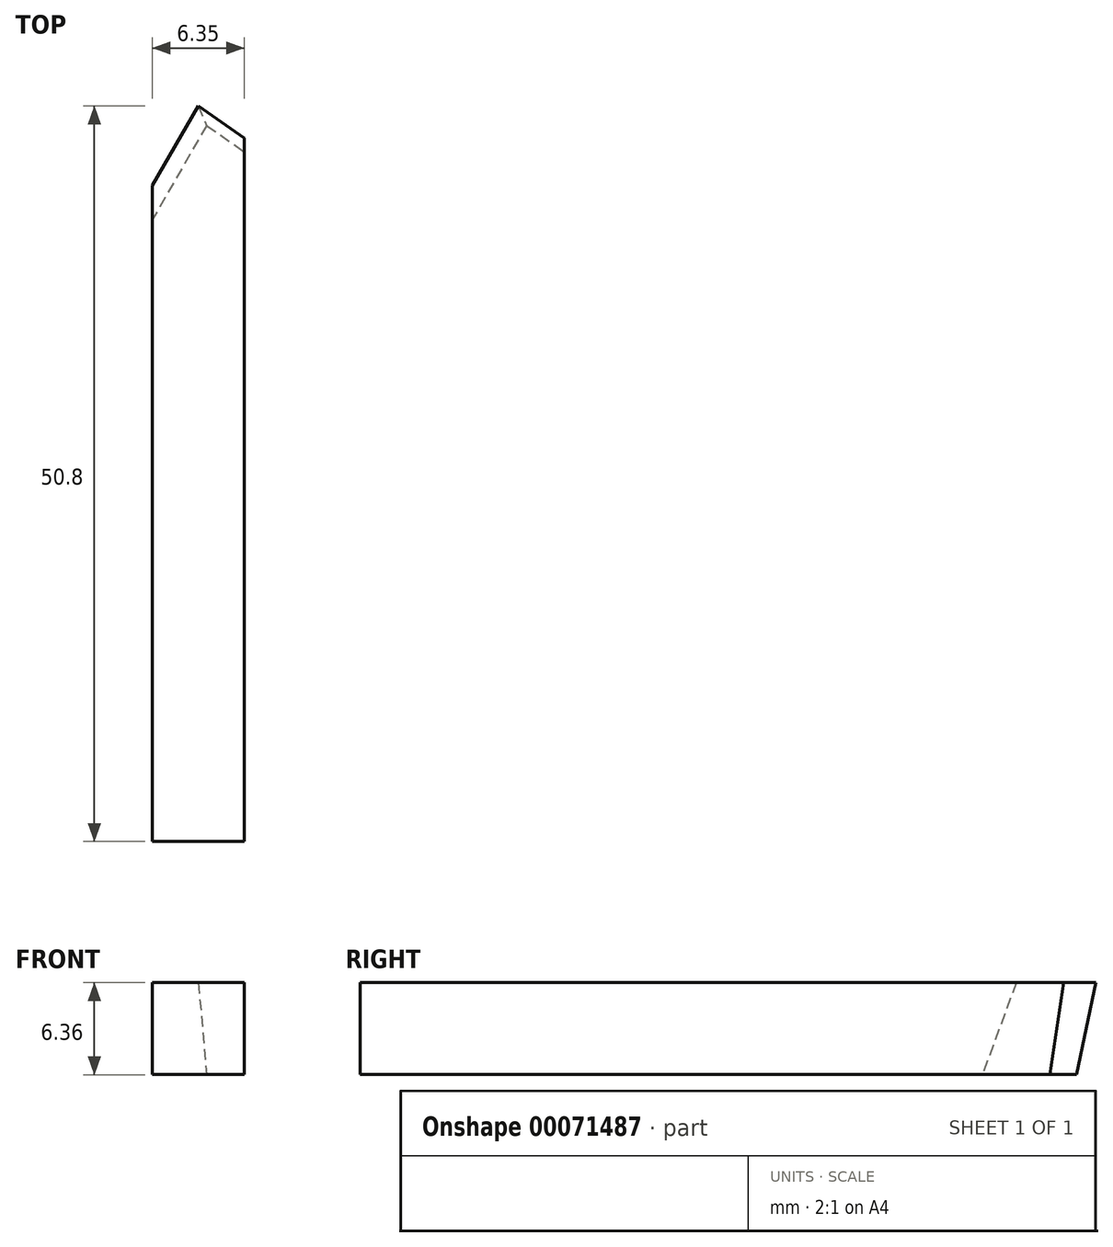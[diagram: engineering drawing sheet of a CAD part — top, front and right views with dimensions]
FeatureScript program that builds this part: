
annotation { "Feature Type Name" : "Feature", "Feature Type Description" : "" }
export const myFeature = defineFeature(function(context is Context, id is Id, definition is map)
    precondition{}
    {
        {
            var Q0;
            Q0=qCreatedBy(makeId("Front.planeOp"),FACE);
            var sketch = newSketch(context, id + "F0", { "sketchPlane" : qUnion([Q0])});
            skLineSegment(sketch, "E0.rect.bottom", {"start": v(3.18, 3.17) * mm, "end": v(-3.18, 3.17) * mm});
            skLineSegment(sketch, "E0.rect.top", {"start": v(3.18, -3.18) * mm, "end": v(-3.18, -3.18) * mm});
            skLineSegment(sketch, "E0.rect.left", {"start": v(3.18, 3.17) * mm, "end": v(3.18, -3.18) * mm});
            skLineSegment(sketch, "E0.rect.right", {"start": v(-3.18, 3.17) * mm, "end": v(-3.18, -3.18) * mm});
            skPoint(sketch, "E0.rect.middle", {"position": v(0, 0) * mm});
            skSolve(sketch);
        }
        {
            var Q0;
            Q0=makeQuery(id+"F0.imprint","IMPRINT",FACE,{"disambiguationData":[TD([[makeQuery(id+"F0.imprint","IMPRINT",EDGE,{"derivedFrom":sQuery(id+"F0.wireOp",EDGE,"E0.rect.bottom")}),1.0]])]});
            extrude(context, id + "F1", {"entities" : qUnion([Q0]), "depth" : 50.8 * mm});
        }
        {
            var Q0;
            Q0=makeQuery(id+"F1.opExtrude","SWEPT_FACE",FACE,{"disambiguationData":[OSD([sQuery(id+"F0.wireOp",EDGE,"E0.rect.bottom")])]});
            var sketch = newSketch(context, id + "F2", { "sketchPlane" : qUnion([Q0])});
            skLineSegment(sketch, "E1", {"start": v(0, 0) * mm, "end": v(-3.18, -5.5) * mm});
            skLineSegment(sketch, "E2", {"start": v(0, 0) * mm, "end": v(3.18, -2.22) * mm});
            skLineSegment(sketch, "E3", {"start": v(3.17, -2.22) * mm, "end": v(3.17, 0) * mm, "construction": true});
            skLineSegment(sketch, "E4", {"start": v(3.17, 0) * mm, "end": v(0, 0) * mm, "construction": true});
            skLineSegment(sketch, "E5", {"start": v(0, 0) * mm, "end": v(-3.18, 0) * mm});
            skLineSegment(sketch, "E6", {"start": v(-3.18, 0) * mm, "end": v(-3.18, -5.5) * mm});
            skSolve(sketch);
        }
        {
            var Q0;
            Q0=makeQuery(id+"F1.opExtrude","CAP_FACE",FACE,{"disambiguationData":[OSD([sQuery(id+"F0.wireOp",EDGE,"E0.rect.bottom"),sQuery(id+"F0.wireOp",EDGE,"E0.rect.top"),sQuery(id+"F0.wireOp",EDGE,"E0.rect.left"),sQuery(id+"F0.wireOp",EDGE,"E0.rect.right")])],"isStart":true});
            var sketch = newSketch(context, id + "F3", { "sketchPlane" : qUnion([Q0])});
            skLineSegment(sketch, "E7", {"start": v(0, 3.17) * mm, "end": v(0, -3.17) * mm});
            skLineSegment(sketch, "E8", {"start": v(0, -3.17) * mm, "end": v(-1.35, -3.18) * mm});
            skLineSegment(sketch, "E9", {"start": v(-1.35, -3.17) * mm, "end": v(0, 3.17) * mm});
            skLineSegment(sketch, "E10", {"start": v(0, 3.17) * mm, "end": v(1.35, -3.17) * mm});
            skLineSegment(sketch, "E11", {"start": v(1.35, -3.17) * mm, "end": v(0, -3.17) * mm});
            skSolve(sketch);
        }
        {
            var Q0;
            Q0=makeQuery(id+"F1.opExtrude","SWEPT_FACE",FACE,{"disambiguationData":[OSD([sQuery(id+"F0.wireOp",EDGE,"E0.rect.bottom")])]});
            var sketch = newSketch(context, id + "F4", { "sketchPlane" : qUnion([Q0])});
            skLineSegment(sketch, "E12", {"start": v(0, 0) * mm, "end": v(-7.35, -12.74) * mm});
            skLineSegment(sketch, "E13", {"start": v(0, 0) * mm, "end": v(31.01, -21.72) * mm});
            skSolve(sketch);
        }
        {
            var Q0;
            Q0=makeQuery(id+"F3.imprint","IMPRINT",FACE,{"disambiguationData":[TD([[makeQuery(id+"F3.imprint","IMPRINT",EDGE,{"derivedFrom":sQuery(id+"F3.wireOp",EDGE,"E7")}),-1.0]])]});
            var Q1;
            Q1=sQuery(id+"F4.wireOp",EDGE,"E12");
            sweep(context, id + "F5", {"operationType" : NewBodyOperationType.REMOVE, "profiles" : qUnion([Q0]), "path" : qUnion([Q1])});
        }
        {
            var Q0;
            Q0=makeQuery(id+"F2.imprint","IMPRINT",FACE,{"disambiguationData":[TD([[makeQuery(id+"F2.imprint","IMPRINT",EDGE,{"derivedFrom":sQuery(id+"F2.wireOp",EDGE,"E1")}),-1.0]])]});
            extrude(context, id + "F6", {"entities" : qUnion([Q0]), "operationType" : NewBodyOperationType.REMOVE, "oppositeDirection" : true, "depth" : 25.4 * mm});
        }
        {
            var Q0;
            Q0=makeQuery(id+"F3.imprint","IMPRINT",FACE,{"disambiguationData":[TD([[makeQuery(id+"F3.imprint","IMPRINT",EDGE,{"derivedFrom":sQuery(id+"F3.wireOp",EDGE,"E7")}),1.0]])]});
            var Q1;
            Q1=sQuery(id+"F4.wireOp",EDGE,"E13");
            sweep(context, id + "F7", {"operationType" : NewBodyOperationType.REMOVE, "profiles" : qUnion([Q0]), "path" : qUnion([Q1])});
        }
        {
            var Q0;
            {var subQ0=sQuery(id+"F4.wireOp",EDGE,"E13");var subQ1=sQuery(id+"F0.wireOp",EDGE,"E0.rect.bottom");var subQ2=makeQuery(id+"F1.opExtrude","CAP_EDGE",EDGE,{"disambiguationData":[OSD([subQ1])],"isStart":true});var subQ3=makeQuery(id+"F4.imprint","INTERSECT",VERTEX,{"derivedFrom":[subQ2,sQuery(id+"F4.wireOp",EDGE,"E12"),subQ0]});Q0=makeQuery(id+"F4.imprint","IMPRINT",FACE,{"disambiguationData":[TD([[makeQuery(id+"F4.imprint","IMPRINT",EDGE,{"disambiguationData":[TD([[subQ3,-1.0]])],"derivedFrom":subQ0}),1.0]])]});}
            extrude(context, id + "F8", {"entities" : qUnion([Q0]), "operationType" : NewBodyOperationType.REMOVE, "oppositeDirection" : true, "depth" : 25.4 * mm});
        }
    });
